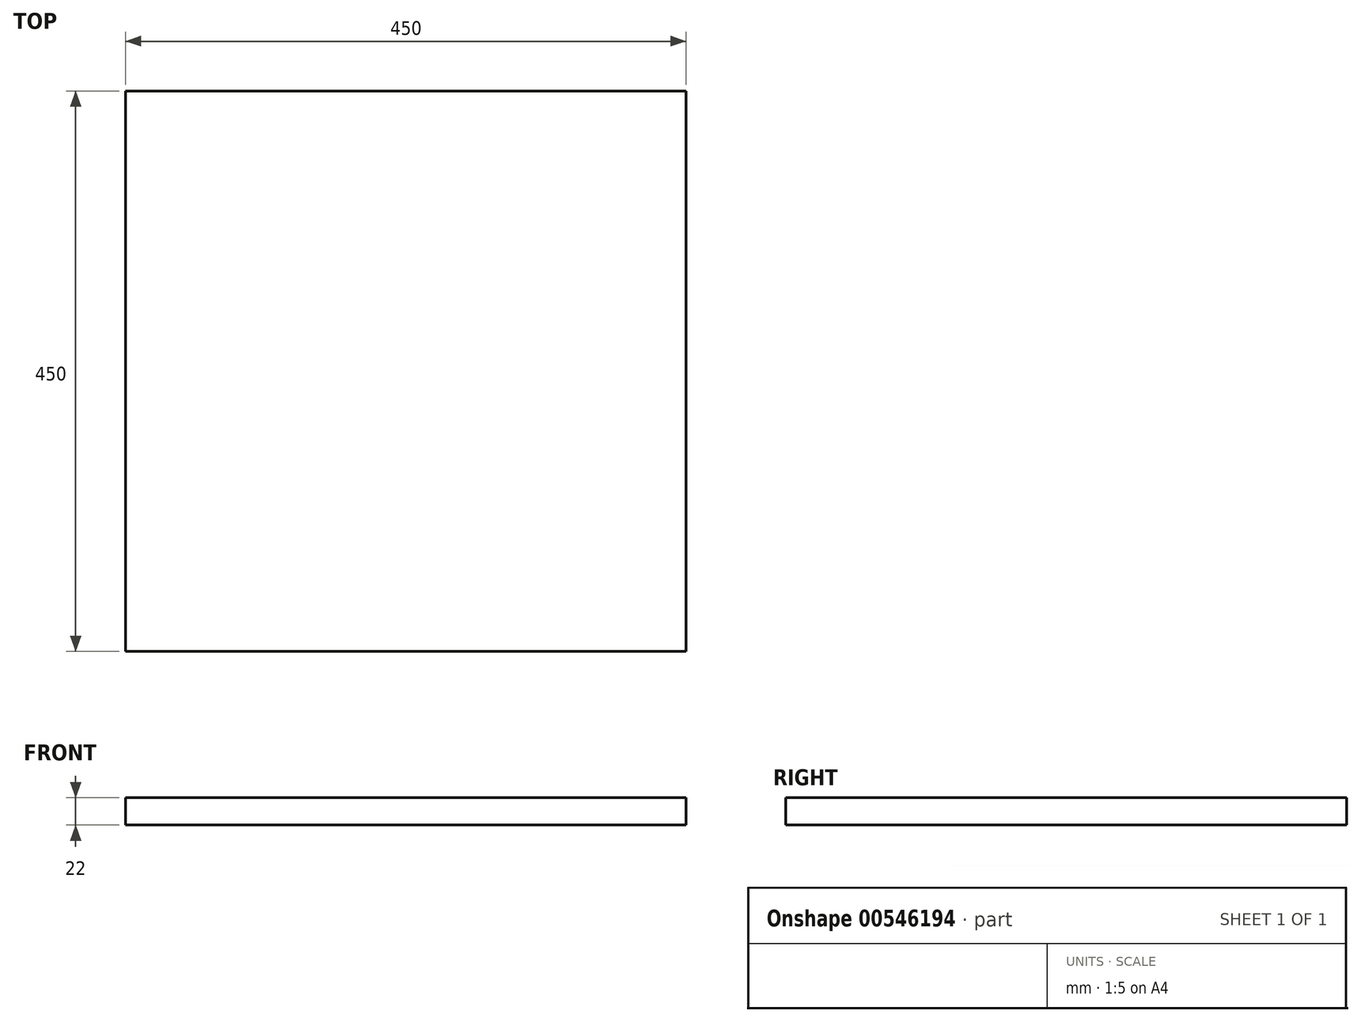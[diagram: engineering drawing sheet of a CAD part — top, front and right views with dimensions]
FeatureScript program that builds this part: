
annotation { "Feature Type Name" : "Feature", "Feature Type Description" : "" }
export const myFeature = defineFeature(function(context is Context, id is Id, definition is map)
    precondition{}
    {
        {
            var Q0;
            Q0=qCreatedBy(makeId("Top.planeOp"),FACE);
            var sketch = newSketch(context, id + "F0", { "sketchPlane" : qUnion([Q0])});
            skLineSegment(sketch, "E0.bottom", {"start": v(0, 0) * mm, "end": v(450, 0) * mm});
            skLineSegment(sketch, "E0.top", {"start": v(0, 450) * mm, "end": v(450, 450) * mm});
            skLineSegment(sketch, "E0.left", {"start": v(0, 0) * mm, "end": v(0, 450) * mm});
            skLineSegment(sketch, "E0.right", {"start": v(450, 0) * mm, "end": v(450, 450) * mm});
            skSolve(sketch);
        }
        {
            var Q0;
            Q0=makeQuery(id+"F0.imprint","IMPRINT",FACE,{"disambiguationData":[TD([[makeQuery(id+"F0.imprint","IMPRINT",EDGE,{"derivedFrom":sQuery(id+"F0.wireOp",EDGE,"E0.bottom")}),1.0]])]});
            extrude(context, id + "F1", {"entities" : qUnion([Q0]), "depth" : 22 * mm, "offsetDistance" : 25 * mm});
        }
    });
